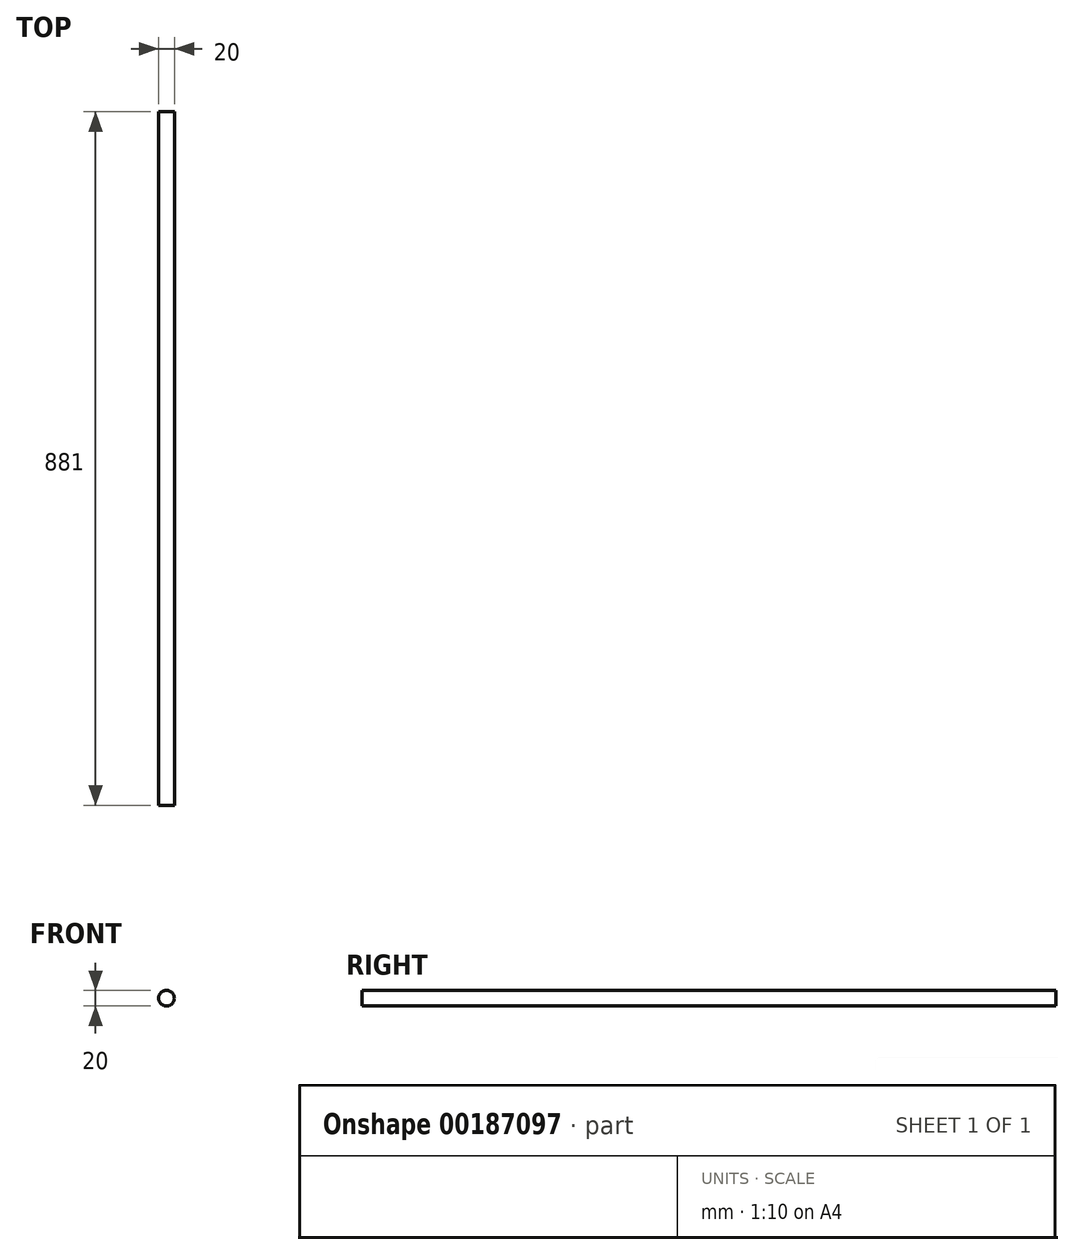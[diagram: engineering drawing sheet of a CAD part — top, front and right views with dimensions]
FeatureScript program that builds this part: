
annotation { "Feature Type Name" : "Feature", "Feature Type Description" : "" }
export const myFeature = defineFeature(function(context is Context, id is Id, definition is map)
    precondition{}
    {
        {
            var Q0;
            Q0=qCreatedBy(makeId("Front.planeOp"),FACE);
            var sketch = newSketch(context, id + "F0", { "sketchPlane" : qUnion([Q0])});
            skCircle(sketch, "E0", {"center": v(0, 0) * mm, "radius": 10 * mm});
            skSolve(sketch);
        }
        {
            var Q0;
            Q0=makeQuery(id+"F0.imprint","IMPRINT",FACE,{"disambiguationData":[TD([[makeQuery(id+"F0.imprint","IMPRINT",EDGE,{"derivedFrom":sQuery(id+"F0.wireOp",EDGE,"E0")}),1.0]])]});
            extrude(context, id + "F1", {"entities" : qUnion([Q0]), "depth" : 881 * mm});
        }
    });
